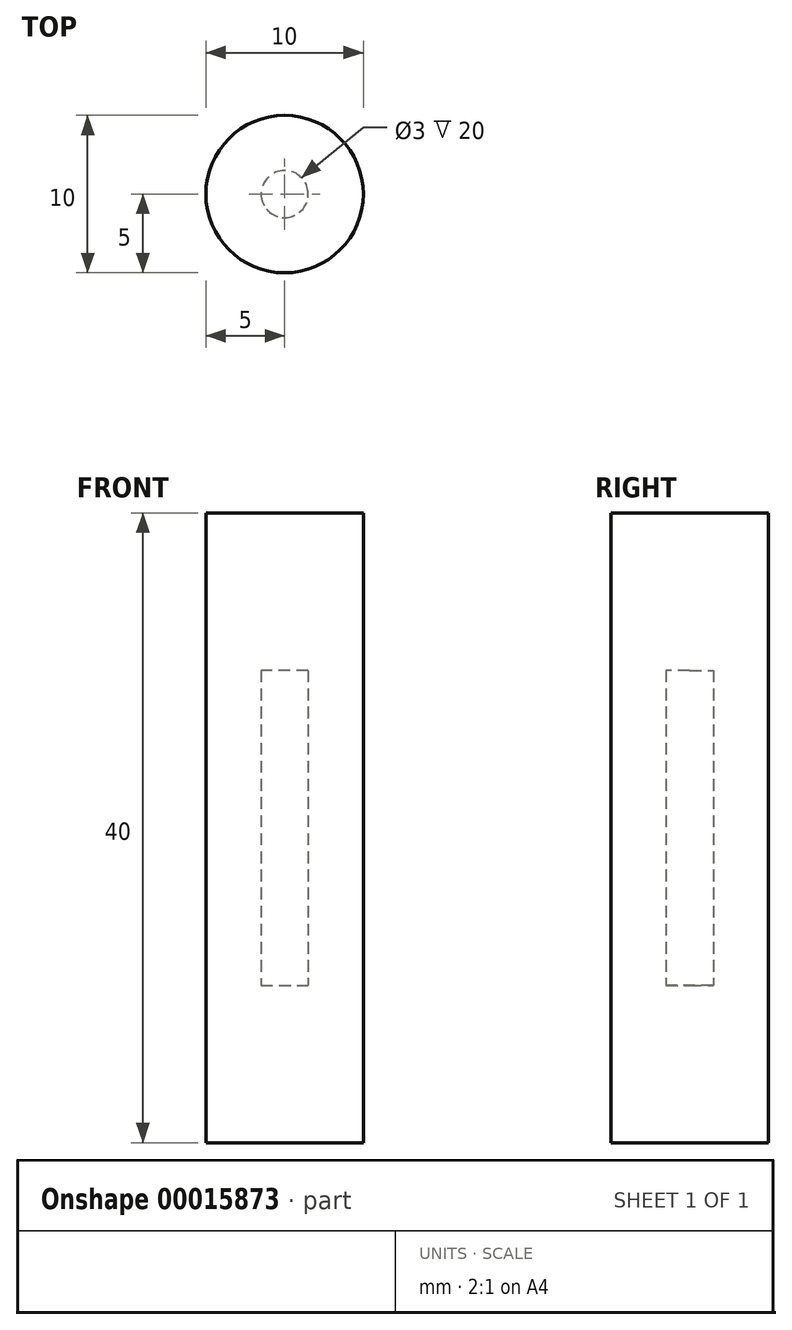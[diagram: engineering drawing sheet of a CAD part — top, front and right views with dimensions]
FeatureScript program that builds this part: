
annotation { "Feature Type Name" : "Feature", "Feature Type Description" : "" }
export const myFeature = defineFeature(function(context is Context, id is Id, definition is map)
    precondition{}
    {
        {
            var Q0;
            Q0=qCreatedBy(makeId("Top.planeOp"),FACE);
            var sketch = newSketch(context, id + "F0", { "sketchPlane" : qUnion([Q0])});
            skCircle(sketch, "E0", {"center": v(0, 0) * mm, "radius": 5 * mm});
            skCircle(sketch, "E1", {"center": v(0, 0) * mm, "radius": 1.5 * mm});
            skSolve(sketch);
        }
        {
            var Q0;
            Q0 = qSketchRegion(id + "F0", true);
            extrude(context, id + "F1", {"entities" : qUnion([Q0]), "depth" : 40 * mm});
        }
        {
            var Q0;
            Q0=makeQuery(id+"F1.opExtrude","CAP_FACE",FACE,{"disambiguationData":[OSD([sQuery(id+"F0.wireOp",EDGE,"E0"),sQuery(id+"F0.wireOp",EDGE,"E1")])],"isStart":false});
            var sketch = newSketch(context, id + "F2", { "sketchPlane" : qUnion([Q0])});
            skCircle(sketch, "E2", {"center": v(0, 0) * mm, "radius": 5 * mm});
            skSolve(sketch);
        }
        {
            var Q0;
            Q0 = qSketchRegion(id + "F2", true);
            extrude(context, id + "F3", {"entities" : qUnion([Q0]), "operationType" : NewBodyOperationType.ADD, "oppositeDirection" : true, "depth" : 10 * mm});
        }
        {
            var Q0;
            Q0=makeQuery(id+"F1.opExtrude","CAP_FACE",FACE,{"disambiguationData":[OSD([sQuery(id+"F0.wireOp",EDGE,"E0"),sQuery(id+"F0.wireOp",EDGE,"E1")])],"isStart":true});
            var sketch = newSketch(context, id + "F4", { "sketchPlane" : qUnion([Q0])});
            skCircle(sketch, "E3", {"center": v(0, 0) * mm, "radius": 5 * mm});
            skSolve(sketch);
        }
        {
            var Q0;
            Q0 = qSketchRegion(id + "F4", true);
            extrude(context, id + "F5", {"entities" : qUnion([Q0]), "operationType" : NewBodyOperationType.ADD, "oppositeDirection" : true, "depth" : 10 * mm});
        }
    });
